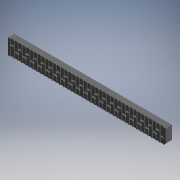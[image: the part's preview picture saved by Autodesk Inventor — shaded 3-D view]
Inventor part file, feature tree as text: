
AUTODESK INVENTOR PART (.ipt)
format: ipt  version: 2017.3 (Build 213256000, 256)  size: 794,624 bytes
history: native  units: mm (DEFAULTED — no unit token found)
features: other x14, extrude x4, sketch x4, pattern_linear x2
ambient origin geometry x8: Origin, YZ Plane, XZ Plane, XY Plane, X Axis, Y Axis, Z Axis, Center Point
bodies: Solid1 (feature_tree)
feature tree (24):
  extrude  "Extrusion1"  Depth=5.08mm TaperAngle=0.0deg
  extrude  "Extrusion2"  Depth=2.54mm TaperAngle=0.0deg
  extrude  "Extrusion3"  Depth=2.54mm TaperAngle=0.0deg
  pattern_linear  "Rectangular Pattern1"  [2 undecoded]
  extrude  "Extrusion4"  [1 undecoded]
  pattern_linear  "Rectangular Pattern2"  [2 undecoded]
  other  "upper_body_to_lower_body_XY"
  other  "upper_body_to_lower_body_YZ"
  other  "upper_body_to_lower_body_ZX"
  other  "upper_body_to_lower_body_X"
  other  "upper_body_to_lower_body_Y"
  other  "upper_body_to_lower_body_Z"
  other  "upper_body_to_lower_body_Center"
  other  "upper_body_to_lower_body_reverse_XY"
  other  "upper_body_to_lower_body_reverse_YZ"
  other  "upper_body_to_lower_body_reverse_ZX"
  other  "upper_body_to_lower_body_reverse_X"
  other  "upper_body_to_lower_body_reverse_Y"
  other  "upper_body_to_lower_body_reverse_Z"
  other  "upper_body_to_lower_body_reverse_Center"
  sketch  "Sketch_1"  dims[d0=2.286mm d1=0.0mm d2=5.08mm d3=0.0mm]
  sketch  "Sketch_7"  dims[d4=1.5748mm d5=0.0mm d6=200.0mm d8=2.54mm d9=10.0mm d11=0.0mm]
  sketch  "Sketch_12"  dims[d12=1.5748mm d13=0.0mm d14=200.0mm d16=2.54mm d17=10.0mm d19=0.0mm]
  sketch  "Sketch_14"  dims[d20=0.0mm d21=0.0mm]
note: 5 required parameter values undecoded (feature->parameter linkage not recoverable at this tier; creation-order binding heuristic only, values carry confidence <= 0.55)
